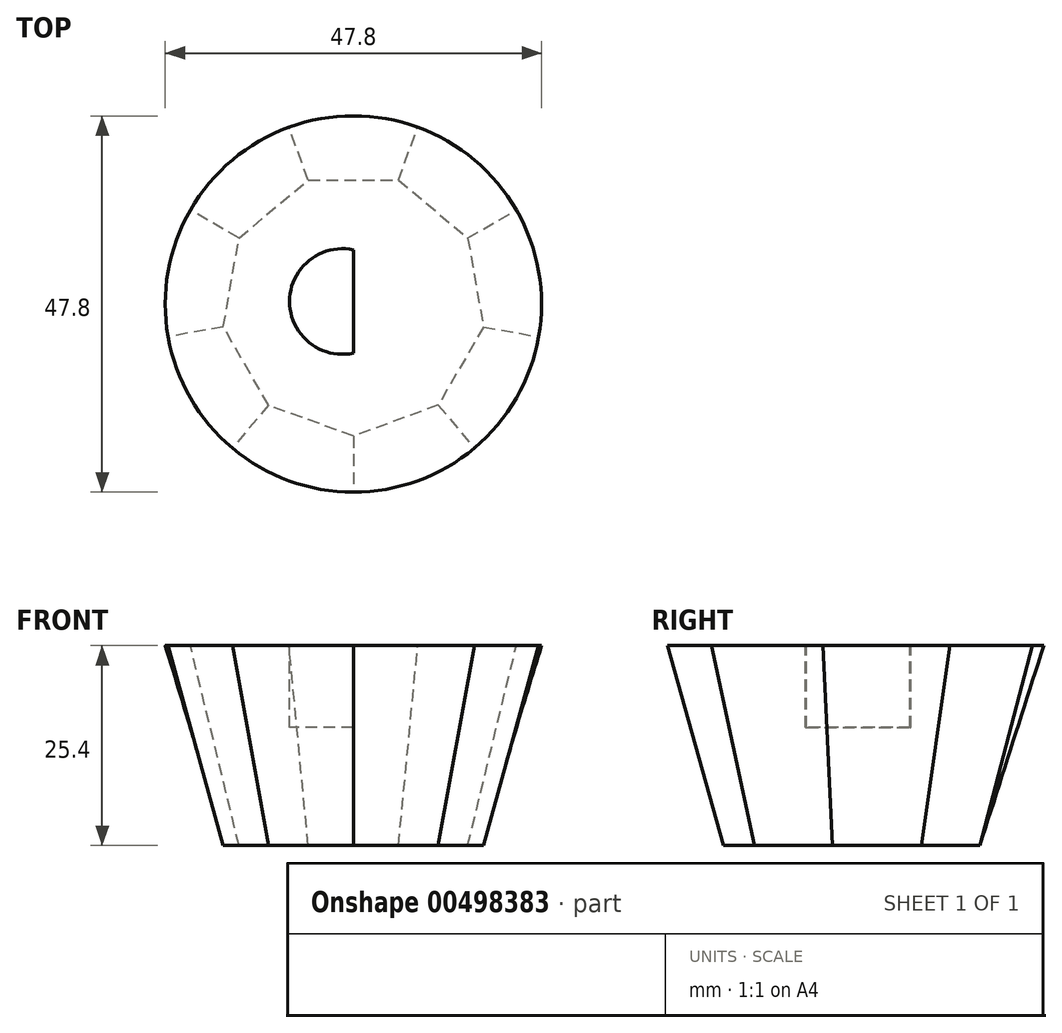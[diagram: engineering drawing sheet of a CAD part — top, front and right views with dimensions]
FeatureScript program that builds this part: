
annotation { "Feature Type Name" : "Feature", "Feature Type Description" : "" }
export const myFeature = defineFeature(function(context is Context, id is Id, definition is map)
    precondition{}
    {
        {
            var Q0;
            Q0=qCreatedBy(makeId("Top.planeOp"),FACE);
            var sketch = newSketch(context, id + "F0", { "sketchPlane" : qUnion([Q0])});
            skCircle(sketch, "E0.cCircle", {"center": v(0, 0) * mm, "radius": 15.76 * mm, "construction": true});
            skLineSegment(sketch, "E0.0", {"start": v(16.52, -2.91) * mm, "end": v(10.78, -12.85) * mm});
            skLineSegment(sketch, "E0.1", {"start": v(10.78, -12.85) * mm, "end": v(0, -16.78) * mm});
            skLineSegment(sketch, "E0.2", {"start": v(0, -16.78) * mm, "end": v(-10.78, -12.85) * mm});
            skLineSegment(sketch, "E0.3", {"start": v(-10.78, -12.85) * mm, "end": v(-16.52, -2.91) * mm});
            skLineSegment(sketch, "E0.4", {"start": v(-16.52, -2.91) * mm, "end": v(-14.53, 8.39) * mm});
            skLineSegment(sketch, "E0.5", {"start": v(-14.53, 8.39) * mm, "end": v(-5.74, 15.76) * mm});
            skLineSegment(sketch, "E0.6", {"start": v(-5.74, 15.76) * mm, "end": v(5.74, 15.76) * mm});
            skLineSegment(sketch, "E0.7", {"start": v(5.74, 15.76) * mm, "end": v(14.53, 8.39) * mm});
            skLineSegment(sketch, "E0.8", {"start": v(14.53, 8.39) * mm, "end": v(16.52, -2.91) * mm});
            skPoint(sketch, "E0.0.midPoint", {"position": v(13.65, -7.88) * mm});
            skSolve(sketch);
        }
        {
            var Q0;
            Q0=makeQuery(id+"F0.imprint","IMPRINT",FACE,{"disambiguationData":[TD([[makeQuery(id+"F0.imprint","IMPRINT",EDGE,{"derivedFrom":sQuery(id+"F0.wireOp",EDGE,"E0.0")}),-1.0]])]});
            cPlane(context, id + "F1", {"entities" : qUnion([Q0]), "cplaneType" : CPlaneType.OFFSET, "offset" : 25.4 * mm, "width" : 152.4 * mm, "height" : 152.4 * mm});
        }
        {
            var Q0;
            Q0=qCreatedBy(id+"F1.planeOp",FACE);
            var sketch = newSketch(context, id + "F2", { "sketchPlane" : qUnion([Q0])});
            skCircle(sketch, "E1", {"center": v(0, 0) * mm, "radius": 23.9 * mm});
            skSolve(sketch);
        }
        {
            var Q0;
            Q0=makeQuery(id+"F0.imprint","IMPRINT",FACE,{"disambiguationData":[TD([[makeQuery(id+"F0.imprint","IMPRINT",EDGE,{"derivedFrom":sQuery(id+"F0.wireOp",EDGE,"E0.0")}),-1.0]])]});
            var Q1;
            Q1=makeQuery(id+"F2.imprint","IMPRINT",FACE,{"disambiguationData":[TD([[makeQuery(id+"F2.imprint","IMPRINT",EDGE,{"derivedFrom":sQuery(id+"F2.wireOp",EDGE,"E1")}),1.0]])]});
            loft(context, id + "F3", {"sheetProfilesArray" : [{ "sheetProfileEntities" : qUnion([Q0]) }, { "sheetProfileEntities" : qUnion([Q1]) }]});
        }
        {
            var Q0;
            Q0=makeQuery(id+"F3.opLoft","CAP_FACE",FACE,{"disambiguationData":[OSD([makeQuery(id+"F2.imprint","IMPRINT",FACE,{"disambiguationData":[TD([[makeQuery(id+"F2.imprint","IMPRINT",EDGE,{"derivedFrom":sQuery(id+"F2.wireOp",EDGE,"E1")}),1.0]])]})])],"isStart":true});
            var sketch = newSketch(context, id + "F4", { "sketchPlane" : qUnion([Q0])});
            skArc(sketch, "E2", {"start": v(0, 6.88) * mm, "mid": v(-8.1, 0.32) * mm, "end": v(0, -6.24) * mm});
            skLineSegment(sketch, "E3", {"start": v(0, -6.24) * mm, "end": v(0, 6.88) * mm});
            skSolve(sketch);
        }
        {
            var Q0;
            Q0=makeQuery(id+"F4.imprint","IMPRINT",FACE,{"disambiguationData":[TD([[makeQuery(id+"F4.imprint","IMPRINT",EDGE,{"derivedFrom":sQuery(id+"F4.wireOp",EDGE,"E2")}),1.0]])]});
            extrude(context, id + "F5", {"entities" : qUnion([Q0]), "operationType" : NewBodyOperationType.REMOVE, "oppositeDirection" : true, "depth" : 10.4 * mm});
        }
    });
